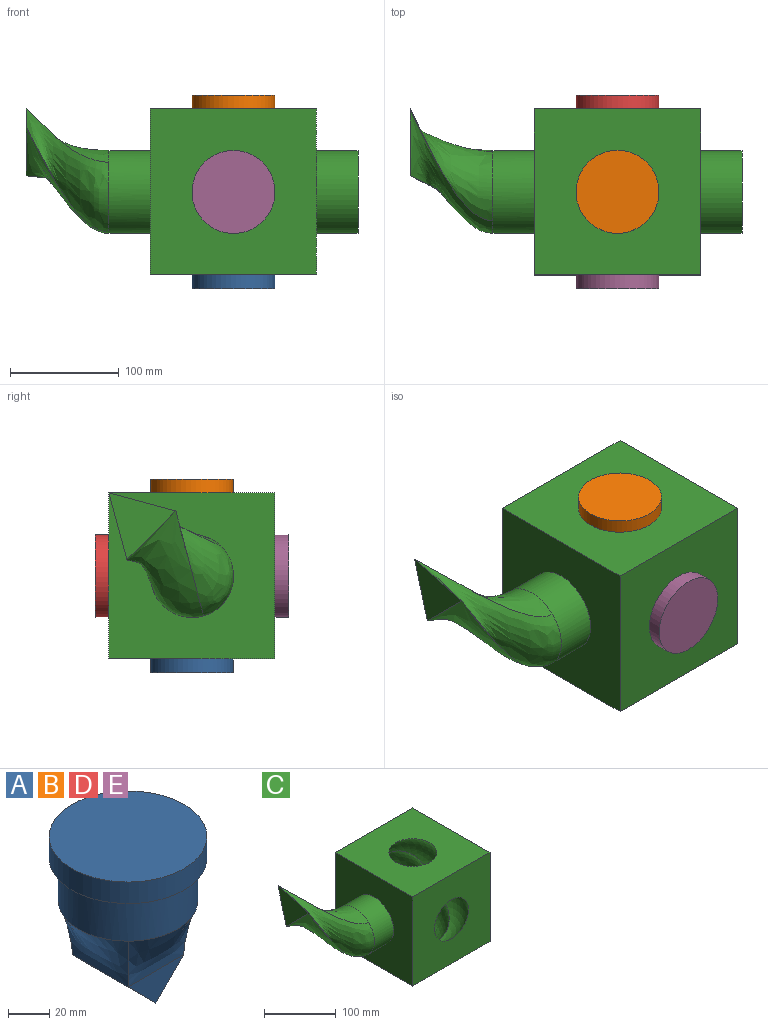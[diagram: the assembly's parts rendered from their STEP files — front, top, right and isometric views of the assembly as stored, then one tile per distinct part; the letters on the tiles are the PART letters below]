
ASSEMBLY  parts=5 mates=1
PART A: 12 faces, bbox 76.2x76.2x88.9 mm
  f0: cylinder r=38.1mm len=76.2mm, axis (0,0,-1), area 3040.2mm2, adj f1,f2
  f1: plane 76.2x76.2mm, normal (0,0,1), area 4560.4mm2, adj f0
  f2: plane 76.2x76.2mm, normal (0,0,-1), area 1012.7mm2, adj f0,f3
  f3: cylinder r=33.6mm len=67.21mm, axis (0,0,1), area 5363mm2, adj f2,f4,f5,f6,f7
  f4: bspline ~47.52x31.75mm, area 1481.2mm2, adj f3,f5,f7,f9
  f5: bspline ~47.52x31.75mm, area 1481.2mm2, adj f3,f4,f6,f11
  f6: bspline ~47.52x31.75mm, area 1481.2mm2, adj f3,f5,f7,f10
  f7: bspline ~47.52x31.75mm, area 1481.2mm2, adj f3,f4,f6,f8
  f8: plane 38.1x19.05mm, normal (0,1,0), area 362.9mm2, adj f7,f9,f10
  f9: plane 38.1x19.05mm, normal (0.71,0,-0.71), area 1026.4mm2, adj f4,f8,f10,f11
  f10: plane 38.1x19.05mm, normal (-0.71,0,-0.71), area 1026.4mm2, adj f6,f8,f9,f11
  f11: plane 38.1x19.05mm, normal (0,-1,0), area 362.9mm2, adj f5,f9,f10
PART B: same geometry as A
PART C: 17 faces, bbox 304.8x177.8x177.8 mm
  f0: plane 152.4x152.4mm, normal (0,1,0), area 19678.8mm2, adj f1,f3,f4,f5,f6
  f1: plane 152.4x152.4mm, normal (-1,0,0), area 18665.4mm2, adj f0,f2,f4,f5,f9
  f2: plane 152.4x152.4mm, normal (0,-1,0), area 19678.8mm2, adj f1,f3,f4,f5,f11
  f3: plane 152.4x152.4mm, normal (1,0,0), area 18665.4mm2, adj f0,f2,f4,f5,f7
  f4: plane 152.4x152.4mm, normal (0,0,1), area 19678.8mm2, adj f0,f1,f2,f3,f10
  f5: plane 152.4x152.4mm, normal (0,0,-1), area 19678.8mm2, adj f0,f1,f2,f3,f12
  f6: sphere r=50.8mm, area 14277.1mm2, adj f0,f10,f12
  f7: cylinder r=38.1mm len=76.2mm, axis (-1,0,0), area 9120.7mm2, adj f3,f8
  f8: plane 76.2x76.2mm, normal (1,0,0), area 4560.4mm2, adj f7
  f9: cylinder r=38.1mm len=76.2mm, axis (1,0,0), area 9120.7mm2, adj f1,f14,f15,f16
  f10: sphere r=50.8mm, area 14277.7mm2, adj f4,f6,f11
  f11: sphere r=50.8mm, area 14277.1mm2, adj f2,f10,f12
  f12: sphere r=50.8mm, area 14277.7mm2, adj f5,f6,f11
  f13: plane 61.34x61.34mm, normal (-1,0,0), area 1746mm2, adj f14,f15,f16
  f14: bspline ~102.65x76.2mm, area 5613mm2, adj f9,f13,f15,f16
  f15: bspline ~114.35x112.82mm, area 5803.3mm2, adj f9,f13,f14,f16
  f16: bspline ~97.92x76.2mm, area 6230.4mm2, adj f9,f13,f14,f15
PART D: same geometry as A
PART E: same geometry as A
PLACE A rot(axis=(0.71,0.71,0),180deg) t=(103.64,0.63,38.75)mm
PLACE B rot(axis=(0,0,-1),90deg) t=(103.64,0.63,191.15)mm
PLACE C t=(103.64,0.63,114.95)mm
PLACE D rot(axis=(-0.58,-0.58,-0.58),120deg) t=(103.64,76.83,114.95)mm
PLACE E rot(axis=(0.58,0.58,-0.58),120deg) t=(103.64,-75.57,114.95)mm
MATE revolute C.f4 <-> B.f3  axis (0,0,1) through (103.64,0.63,191.15)mm
